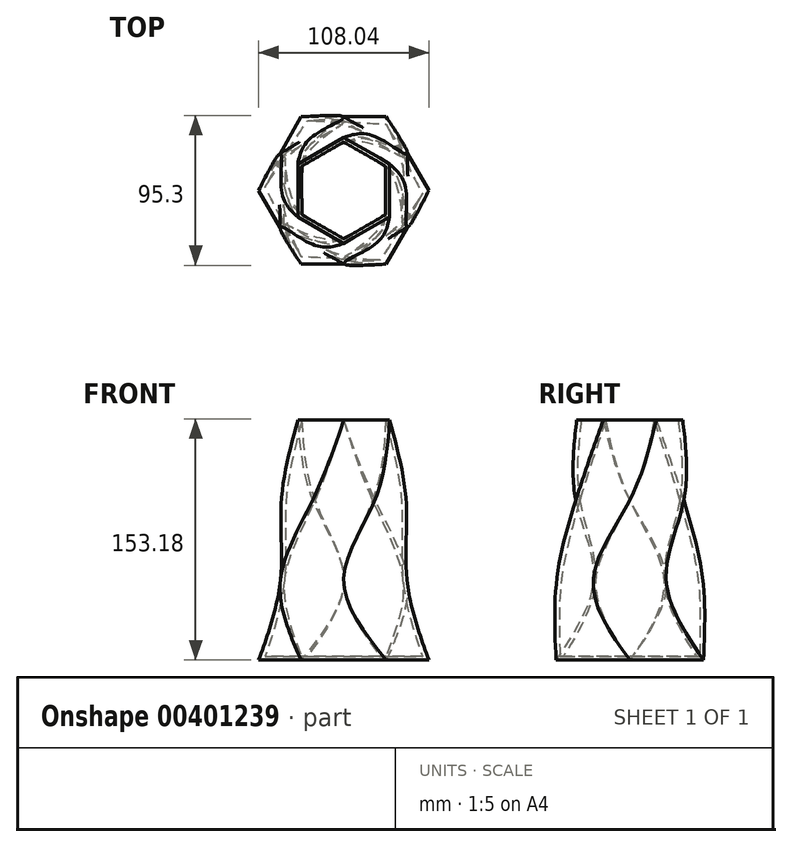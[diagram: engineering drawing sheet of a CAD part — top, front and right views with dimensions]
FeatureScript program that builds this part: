
annotation { "Feature Type Name" : "Feature", "Feature Type Description" : "" }
export const myFeature = defineFeature(function(context is Context, id is Id, definition is map)
    precondition{}
    {
        {
            var Q0;
            Q0=qCreatedBy(makeId("Top.planeOp"),FACE);
            var sketch = newSketch(context, id + "F0", { "sketchPlane" : qUnion([Q0])});
            skCircle(sketch, "E0.cCircle", {"center": v(0, 0) * mm, "radius": 46.78 * mm, "construction": true});
            skLineSegment(sketch, "E0.0", {"start": v(27.01, -46.78) * mm, "end": v(-27.01, -46.78) * mm});
            skLineSegment(sketch, "E0.1", {"start": v(-27.01, -46.78) * mm, "end": v(-54.02, 0) * mm});
            skLineSegment(sketch, "E0.2", {"start": v(-54.02, 0) * mm, "end": v(-27.01, 46.78) * mm});
            skLineSegment(sketch, "E0.3", {"start": v(-27.01, 46.78) * mm, "end": v(27.01, 46.78) * mm});
            skLineSegment(sketch, "E0.4", {"start": v(27.01, 46.78) * mm, "end": v(54.02, 0) * mm});
            skLineSegment(sketch, "E0.5", {"start": v(54.02, 0) * mm, "end": v(27.01, -46.78) * mm});
            skPoint(sketch, "E0.0.midPoint", {"position": v(0, -46.78) * mm});
            skSolve(sketch);
        }
        {
            var Q0;
            Q0=qCreatedBy(makeId("Top.planeOp"),FACE);
            cPlane(context, id + "F1", {"entities" : qUnion([Q0]), "cplaneType" : CPlaneType.OFFSET, "offset" : 50.8 * mm, "width" : 152.4 * mm, "height" : 152.4 * mm});
        }
        {
            var Q0;
            Q0=qCreatedBy(id+"F1.planeOp",FACE);
            var sketch = newSketch(context, id + "F2", { "sketchPlane" : qUnion([Q0])});
            skCircle(sketch, "E1.cCircle", {"center": v(0, 0) * mm, "radius": 40.16 * mm, "construction": true});
            skLineSegment(sketch, "E1.0", {"start": v(40.16, 23.19) * mm, "end": v(40.16, -23.19) * mm});
            skLineSegment(sketch, "E1.1", {"start": v(40.16, -23.19) * mm, "end": v(0, -46.37) * mm});
            skLineSegment(sketch, "E1.2", {"start": v(0, -46.37) * mm, "end": v(-40.16, -23.19) * mm});
            skLineSegment(sketch, "E1.3", {"start": v(-40.16, -23.19) * mm, "end": v(-40.16, 23.19) * mm});
            skLineSegment(sketch, "E1.4", {"start": v(-40.16, 23.19) * mm, "end": v(0, 46.37) * mm});
            skLineSegment(sketch, "E1.5", {"start": v(0, 46.37) * mm, "end": v(40.16, 23.19) * mm});
            skPoint(sketch, "E1.0.midPoint", {"position": v(40.16, 0) * mm});
            skSolve(sketch);
        }
        {
            var Q0;
            Q0=qCreatedBy(id+"F1.planeOp",FACE);
            cPlane(context, id + "F3", {"entities" : qUnion([Q0]), "cplaneType" : CPlaneType.OFFSET, "offset" : 50.8 * mm, "width" : 150 * mm, "height" : 150 * mm});
        }
        {
            var Q0;
            Q0=qCreatedBy(id+"F3.planeOp",FACE);
            var sketch = newSketch(context, id + "F4", { "sketchPlane" : qUnion([Q0])});
            skCircle(sketch, "E2.cCircle", {"center": v(0, 0) * mm, "radius": 34.27 * mm, "construction": true});
            skLineSegment(sketch, "E2.0", {"start": v(-19.79, 34.27) * mm, "end": v(19.79, 34.27) * mm});
            skLineSegment(sketch, "E2.1", {"start": v(19.79, 34.27) * mm, "end": v(39.58, 0) * mm});
            skLineSegment(sketch, "E2.2", {"start": v(39.58, 0) * mm, "end": v(19.79, -34.27) * mm});
            skLineSegment(sketch, "E2.3", {"start": v(19.79, -34.27) * mm, "end": v(-19.79, -34.27) * mm});
            skLineSegment(sketch, "E2.4", {"start": v(-19.79, -34.27) * mm, "end": v(-39.58, 0) * mm});
            skLineSegment(sketch, "E2.5", {"start": v(-39.58, 0) * mm, "end": v(-19.79, 34.27) * mm});
            skPoint(sketch, "E2.0.midPoint", {"position": v(0, 34.27) * mm});
            skSolve(sketch);
        }
        {
            var Q0;
            Q0=qCreatedBy(id+"F3.planeOp",FACE);
            cPlane(context, id + "F5", {"entities" : qUnion([Q0]), "cplaneType" : CPlaneType.OFFSET, "offset" : 50.8 * mm, "width" : 150 * mm, "height" : 150 * mm});
        }
        {
            var Q0;
            Q0=qCreatedBy(id+"F5.planeOp",FACE);
            var sketch = newSketch(context, id + "F6", { "sketchPlane" : qUnion([Q0])});
            skCircle(sketch, "E3.cCircle", {"center": v(0, 0) * mm, "radius": 29.17 * mm, "construction": true});
            skLineSegment(sketch, "E3.0", {"start": v(-29.17, -16.84) * mm, "end": v(-29.17, 16.84) * mm});
            skLineSegment(sketch, "E3.1", {"start": v(-29.17, 16.84) * mm, "end": v(0, 33.68) * mm});
            skLineSegment(sketch, "E3.2", {"start": v(0, 33.68) * mm, "end": v(29.17, 16.84) * mm});
            skLineSegment(sketch, "E3.3", {"start": v(29.17, 16.84) * mm, "end": v(29.17, -16.84) * mm});
            skLineSegment(sketch, "E3.4", {"start": v(29.17, -16.84) * mm, "end": v(0, -33.68) * mm});
            skLineSegment(sketch, "E3.5", {"start": v(0, -33.68) * mm, "end": v(-29.17, -16.84) * mm});
            skPoint(sketch, "E3.0.midPoint", {"position": v(-29.17, 0) * mm});
            skSolve(sketch);
        }
        {
            var Q0;
            Q0=makeQuery(id+"F6.imprint","IMPRINT",FACE,{"disambiguationData":[TD([[makeQuery(id+"F6.imprint","IMPRINT",EDGE,{"derivedFrom":sQuery(id+"F6.wireOp",EDGE,"E3.0")}),-1.0]])]});
            var Q1;
            Q1=makeQuery(id+"F4.imprint","IMPRINT",FACE,{"disambiguationData":[TD([[makeQuery(id+"F4.imprint","IMPRINT",EDGE,{"derivedFrom":sQuery(id+"F4.wireOp",EDGE,"E2.0")}),-1.0]])]});
            var Q2;
            Q2=makeQuery(id+"F2.imprint","IMPRINT",FACE,{"disambiguationData":[TD([[makeQuery(id+"F2.imprint","IMPRINT",EDGE,{"derivedFrom":sQuery(id+"F2.wireOp",EDGE,"E1.0")}),-1.0]])]});
            var Q3;
            Q3=makeQuery(id+"F0.imprint","IMPRINT",FACE,{"disambiguationData":[TD([[makeQuery(id+"F0.imprint","IMPRINT",EDGE,{"derivedFrom":sQuery(id+"F0.wireOp",EDGE,"E0.0")}),-1.0]])]});
            loft(context, id + "F7", {"sheetProfilesArray" : [{ "sheetProfileEntities" : qUnion([Q0]) }, { "sheetProfileEntities" : qUnion([Q1]) }, { "sheetProfileEntities" : qUnion([Q2]) }, { "sheetProfileEntities" : qUnion([Q3]) }]});
        }
        {
            var Q0;
            Q0=makeQuery(id+"F7.opLoft","CAP_FACE",FACE,{"disambiguationData":[OSD([makeQuery(id+"F6.imprint","IMPRINT",FACE,{"disambiguationData":[TD([[makeQuery(id+"F6.imprint","IMPRINT",EDGE,{"derivedFrom":sQuery(id+"F6.wireOp",EDGE,"E3.0")}),-1.0]])]})])],"isStart":true});
            shell(context, id + "F8", {"entities" : qUnion([Q0]), "thickness" : 2.5 * mm});
        }
    });
